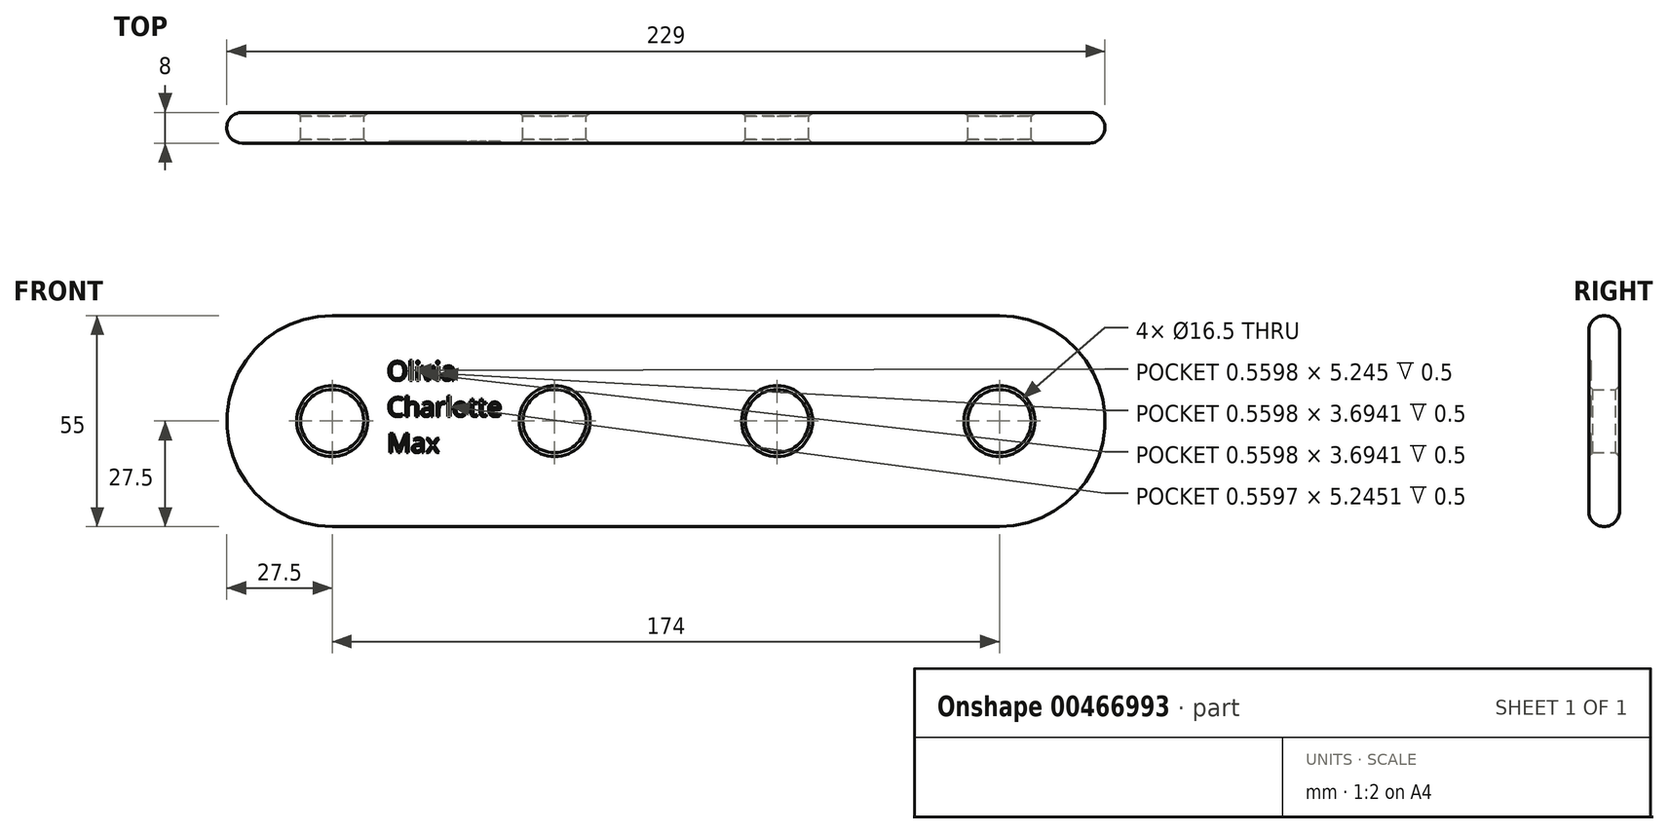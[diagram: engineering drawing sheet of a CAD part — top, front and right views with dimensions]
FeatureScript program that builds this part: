
annotation { "Feature Type Name" : "Feature", "Feature Type Description" : "" }
export const myFeature = defineFeature(function(context is Context, id is Id, definition is map)
    precondition{}
    {
        {
            var Q0;
            Q0=qCreatedBy(makeId("Front.planeOp"),FACE);
            var sketch = newSketch(context, id + "F0", { "sketchPlane" : qUnion([Q0])});
            skLineSegment(sketch, "E0.bottom", {"start": v(0, 0) * mm, "end": v(174, 0) * mm});
            skLineSegment(sketch, "E0.top", {"start": v(0, 55) * mm, "end": v(174, 55) * mm});
            skArc(sketch, "E1", {"start": v(174, 0) * mm, "mid": v(201.5, 27.5) * mm, "end": v(174, 55) * mm});
            skArc(sketch, "E2", {"start": v(0, 55) * mm, "mid": v(-27.5, 27.5) * mm, "end": v(0, 0) * mm});
            skLineSegment(sketch, "E3", {"start": v(174, 27.5) * mm, "end": v(0, 27.5) * mm, "construction": true});
            skCircle(sketch, "E4", {"center": v(0, 27.5) * mm, "radius": 8.25 * mm});
            skCircle(sketch, "E5.1.0.0", {"center": v(58, 27.5) * mm, "radius": 8.25 * mm});
            skCircle(sketch, "E5.2.0.0", {"center": v(116, 27.5) * mm, "radius": 8.25 * mm});
            skCircle(sketch, "E5.3.0.0", {"center": v(174, 27.5) * mm, "radius": 8.25 * mm});
            skLineSegment(sketch, "E5.direction1", {"start": v(0, 27.5) * mm, "end": v(58, 27.5) * mm, "construction": true});
            skSolve(sketch);
        }
        {
            var Q0;
            Q0=makeQuery(id+"F0.imprint","IMPRINT",FACE,{"disambiguationData":[TD([[makeQuery(id+"F0.imprint","IMPRINT",EDGE,{"derivedFrom":sQuery(id+"F0.wireOp",EDGE,"E0.bottom")}),1.0]])]});
            extrude(context, id + "F1", {"entities" : qUnion([Q0]), "depth" : 8 * mm});
        }
        {
            var Q0;
            Q0=makeQuery(id+"F1.opExtrude","CAP_EDGE",EDGE,{"disambiguationData":[OSD([sQuery(id+"F0.wireOp",EDGE,"E0.top")])],"isStart":false});
            var Q1;
            Q1=makeQuery(id+"F1.opExtrude","CAP_EDGE",EDGE,{"disambiguationData":[OSD([sQuery(id+"F0.wireOp",EDGE,"E0.top")])],"isStart":true});
            fillet(context, id + "F2", {"entities" : qUnion([Q0, Q1]), "radius" : 4 * mm, "tangentPropagation" : true, "allowEdgeOverflow" : false});
        }
        {
            var Q0;
            Q0=makeQuery(id+"F1.opExtrude","CAP_EDGE",EDGE,{"disambiguationData":[OSD([sQuery(id+"F0.wireOp",EDGE,"E5.3.0.0")])],"isStart":true});
            var Q1;
            Q1=makeQuery(id+"F1.opExtrude","CAP_EDGE",EDGE,{"disambiguationData":[OSD([sQuery(id+"F0.wireOp",EDGE,"E5.2.0.0")])],"isStart":true});
            var Q2;
            Q2=makeQuery(id+"F1.opExtrude","CAP_EDGE",EDGE,{"disambiguationData":[OSD([sQuery(id+"F0.wireOp",EDGE,"E5.1.0.0")])],"isStart":true});
            var Q3;
            Q3=makeQuery(id+"F1.opExtrude","CAP_EDGE",EDGE,{"disambiguationData":[OSD([sQuery(id+"F0.wireOp",EDGE,"E4")])],"isStart":true});
            var Q4;
            Q4=makeQuery(id+"F1.opExtrude","CAP_EDGE",EDGE,{"disambiguationData":[OSD([sQuery(id+"F0.wireOp",EDGE,"E4")])],"isStart":false});
            var Q5;
            Q5=makeQuery(id+"F1.opExtrude","CAP_EDGE",EDGE,{"disambiguationData":[OSD([sQuery(id+"F0.wireOp",EDGE,"E5.1.0.0")])],"isStart":false});
            var Q6;
            Q6=makeQuery(id+"F1.opExtrude","CAP_EDGE",EDGE,{"disambiguationData":[OSD([sQuery(id+"F0.wireOp",EDGE,"E5.2.0.0")])],"isStart":false});
            var Q7;
            Q7=makeQuery(id+"F1.opExtrude","CAP_EDGE",EDGE,{"disambiguationData":[OSD([sQuery(id+"F0.wireOp",EDGE,"E5.3.0.0")])],"isStart":false});
            chamfer(context, id + "F3", {"entities" : qUnion([Q0, Q1, Q2, Q3, Q4, Q5, Q6, Q7]), "width" : 1 * mm, "tangentPropagation" : true});
        }
        {
            var Q0;
            Q0=makeQuery(id+"F1.opExtrude","CAP_FACE",FACE,{"disambiguationData":[OSD([sQuery(id+"F0.wireOp",EDGE,"E0.bottom"),sQuery(id+"F0.wireOp",EDGE,"E0.top"),sQuery(id+"F0.wireOp",EDGE,"E1"),sQuery(id+"F0.wireOp",EDGE,"E2"),sQuery(id+"F0.wireOp",EDGE,"E4"),sQuery(id+"F0.wireOp",EDGE,"E5.1.0.0"),sQuery(id+"F0.wireOp",EDGE,"E5.2.0.0"),sQuery(id+"F0.wireOp",EDGE,"E5.3.0.0")])],"isStart":false});
            var sketch = newSketch(context, id + "F4", { "sketchPlane" : qUnion([Q0])});
            skText(sketch, "E6", { "text": "Olivia\nCharlotte\nMax", "fontName": "OpenSans-Regular.ttf"});
            const initialGuessF4  = {"E6": [0.01433, 0.03812, 1, 0, 0.00497]};
            skSetInitialGuess(sketch, initialGuessF4);
            skSolve(sketch);
        }
        {
            var Q0;
            Q0 = qSketchRegion(id + "F4", true);
            extrude(context, id + "F5", {"entities" : qUnion([Q0]), "operationType" : NewBodyOperationType.REMOVE, "oppositeDirection" : true, "depth" : 0.5 * mm});
        }
    });
